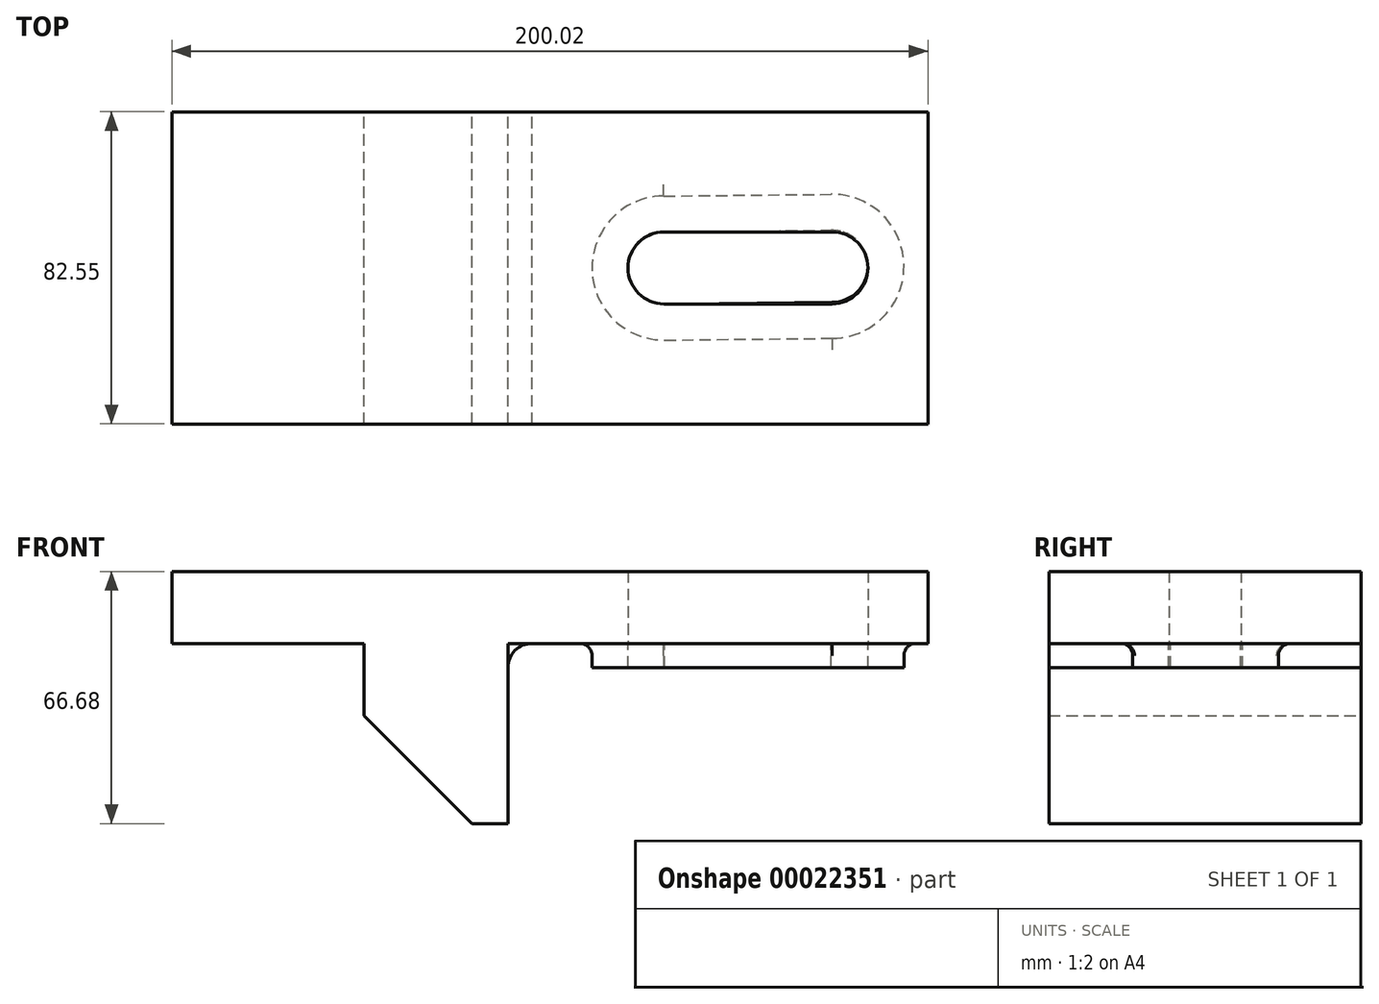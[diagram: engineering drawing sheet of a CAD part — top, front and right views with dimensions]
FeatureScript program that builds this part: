
annotation { "Feature Type Name" : "Feature", "Feature Type Description" : "" }
export const myFeature = defineFeature(function(context is Context, id is Id, definition is map)
    precondition{}
    {
        {
            var Q0;
            Q0=qCreatedBy(makeId("Top.planeOp"),FACE);
            var sketch = newSketch(context, id + "F0", { "sketchPlane" : qUnion([Q0])});
            skLineSegment(sketch, "E0.bottom", {"start": v(-105.1, 26.86) * mm, "end": v(94.93, 26.86) * mm});
            skLineSegment(sketch, "E0.top", {"start": v(-105.1, -55.7) * mm, "end": v(94.93, -55.7) * mm});
            skLineSegment(sketch, "E0.left", {"start": v(-105.1, 26.86) * mm, "end": v(-105.1, -55.7) * mm});
            skLineSegment(sketch, "E0.right", {"start": v(94.93, 26.86) * mm, "end": v(94.93, -55.7) * mm});
            skLineSegment(sketch, "E1.bottom", {"start": v(25.08, 4.63) * mm, "end": v(69.53, 4.63) * mm});
            skLineSegment(sketch, "E1.top", {"start": v(25.08, -33.47) * mm, "end": v(69.53, -33.47) * mm});
            skLineSegment(sketch, "E1.left", {"start": v(25.08, 4.63) * mm, "end": v(25.08, -33.47) * mm});
            skLineSegment(sketch, "E1.right", {"start": v(69.53, 4.63) * mm, "end": v(69.53, -33.47) * mm});
            skLineSegment(sketch, "E2.bottom", {"start": v(25.08, -4.9) * mm, "end": v(69.53, -4.9) * mm});
            skLineSegment(sketch, "E2.top", {"start": v(25.08, -23.94) * mm, "end": v(69.53, -23.94) * mm});
            skLineSegment(sketch, "E2.left", {"start": v(25.08, -4.9) * mm, "end": v(25.08, -23.94) * mm});
            skLineSegment(sketch, "E2.right", {"start": v(69.53, -4.9) * mm, "end": v(69.53, -23.94) * mm});
            skCircle(sketch, "E3", {"center": v(69.53, -14.42) * mm, "radius": 19.05 * mm});
            skCircle(sketch, "E4", {"center": v(25.08, -14.42) * mm, "radius": 19.05 * mm});
            skCircle(sketch, "E5", {"center": v(25.08, -14.42) * mm, "radius": 9.53 * mm});
            skCircle(sketch, "E6", {"center": v(69.53, -14.42) * mm, "radius": 9.53 * mm});
            skSolve(sketch);
        }
        {
            var Q0;
            Q0 = qSketchRegion(id + "F0", true);
            var Q1;
            {var subQ1=sQuery(id+"F0.wireOp",EDGE,"E1.left");var subQ5=sQuery(id+"F0.wireOp",EDGE,"E4");var subQ7=makeQuery(id+"F0.imprint","INTERSECT",VERTEX,{"derivedFrom":[sQuery(id+"F0.wireOp",EDGE,"E1.bottom"),subQ1,subQ5]});Q1=makeQuery(id+"F0.imprint","IMPRINT",FACE,{"disambiguationData":[TD([[makeQuery(id+"F0.imprint","IMPRINT",EDGE,{"disambiguationData":[TD([[subQ7,-1.0]])],"derivedFrom":subQ5}),1.0]])]});}
            var Q2;
            {var subQ3=sQuery(id+"F0.wireOp",EDGE,"E1.bottom");Q2=makeQuery(id+"F0.imprint","IMPRINT",FACE,{"disambiguationData":[TD([[makeQuery(id+"F0.imprint","IMPRINT",EDGE,{"derivedFrom":subQ3}),-1.0]])]});}
            var Q3;
            {var subQ1=sQuery(id+"F0.wireOp",EDGE,"E1.right");var subQ5=sQuery(id+"F0.wireOp",EDGE,"E3");var subQ7=makeQuery(id+"F0.imprint","INTERSECT",VERTEX,{"derivedFrom":[sQuery(id+"F0.wireOp",EDGE,"E1.bottom"),subQ1,subQ5]});Q3=makeQuery(id+"F0.imprint","IMPRINT",FACE,{"disambiguationData":[TD([[makeQuery(id+"F0.imprint","IMPRINT",EDGE,{"disambiguationData":[TD([[subQ7,1.0]])],"derivedFrom":subQ5}),1.0]])]});}
            var Q4;
            {var subQ0=sQuery(id+"F0.wireOp",EDGE,"E3");var subQ1=sQuery(id+"F0.wireOp",EDGE,"E2.bottom");var subQ2=makeQuery(id+"F0.imprint","INTERSECT",VERTEX,{"derivedFrom":[subQ1,subQ0]});Q4=makeQuery(id+"F0.imprint","IMPRINT",FACE,{"disambiguationData":[TD([[makeQuery(id+"F0.imprint","IMPRINT",EDGE,{"disambiguationData":[TD([[subQ2,1.0]])],"derivedFrom":subQ0}),1.0]])]});}
            var Q5;
            {var subQ0=sQuery(id+"F0.wireOp",EDGE,"E4");var subQ1=sQuery(id+"F0.wireOp",EDGE,"E2.bottom");var subQ2=makeQuery(id+"F0.imprint","INTERSECT",VERTEX,{"derivedFrom":[subQ1,subQ0]});Q5=makeQuery(id+"F0.imprint","IMPRINT",FACE,{"disambiguationData":[TD([[makeQuery(id+"F0.imprint","IMPRINT",EDGE,{"disambiguationData":[TD([[subQ2,-1.0]])],"derivedFrom":subQ0}),1.0]])]});}
            var Q6;
            {var subQ0=sQuery(id+"F0.wireOp",EDGE,"E4");var subQ1=sQuery(id+"F0.wireOp",EDGE,"E2.top");var subQ2=makeQuery(id+"F0.imprint","INTERSECT",VERTEX,{"derivedFrom":[subQ1,subQ0]});Q6=makeQuery(id+"F0.imprint","IMPRINT",FACE,{"disambiguationData":[TD([[makeQuery(id+"F0.imprint","IMPRINT",EDGE,{"disambiguationData":[TD([[subQ2,1.0]])],"derivedFrom":subQ0}),1.0]])]});}
            var Q7;
            {var subQ3=sQuery(id+"F0.wireOp",EDGE,"E1.top");Q7=makeQuery(id+"F0.imprint","IMPRINT",FACE,{"disambiguationData":[TD([[makeQuery(id+"F0.imprint","IMPRINT",EDGE,{"derivedFrom":subQ3}),1.0]])]});}
            var Q8;
            {var subQ0=sQuery(id+"F0.wireOp",EDGE,"E3");var subQ1=sQuery(id+"F0.wireOp",EDGE,"E2.top");var subQ2=makeQuery(id+"F0.imprint","INTERSECT",VERTEX,{"derivedFrom":[subQ1,subQ0]});Q8=makeQuery(id+"F0.imprint","IMPRINT",FACE,{"disambiguationData":[TD([[makeQuery(id+"F0.imprint","IMPRINT",EDGE,{"disambiguationData":[TD([[subQ2,-1.0]])],"derivedFrom":subQ0}),1.0]])]});}
            extrude(context, id + "F1", {"entities" : qUnion([Q0, Q1, Q2, Q3, Q4, Q5, Q6, Q7, Q8]), "depth" : 19.05 * mm});
        }
        {
            var Q0;
            Q0=qCreatedBy(makeId("Top.planeOp"),FACE);
            var sketch = newSketch(context, id + "F2", { "sketchPlane" : qUnion([Q0])});
            skCircle(sketch, "E7", {"center": v(25.08, -14.47) * mm, "radius": 19.05 * mm});
            skCircle(sketch, "E8", {"center": v(69.53, -14) * mm, "radius": 19.05 * mm});
            skLineSegment(sketch, "E9", {"start": v(25.05, 4.58) * mm, "end": v(69.34, 5.04) * mm});
            skLineSegment(sketch, "E10", {"start": v(25.3, -33.52) * mm, "end": v(69.54, -33.06) * mm});
            skLineSegment(sketch, "E11", {"start": v(25.08, -24) * mm, "end": v(25.3, -33.52) * mm});
            skLineSegment(sketch, "E12", {"start": v(25.08, -4.94) * mm, "end": v(25.05, 4.58) * mm});
            skLineSegment(sketch, "E13", {"start": v(69.34, 5.04) * mm, "end": v(69.53, -4.48) * mm});
            skLineSegment(sketch, "E14", {"start": v(69.54, -33.06) * mm, "end": v(69.53, -23.53) * mm});
            skLineSegment(sketch, "E15", {"start": v(25.08, -24) * mm, "end": v(69.53, -23.53) * mm});
            skLineSegment(sketch, "E16", {"start": v(25.08, -4.94) * mm, "end": v(69.53, -4.48) * mm});
            skCircle(sketch, "E17", {"center": v(25.08, -14.47) * mm, "radius": 9.53 * mm});
            skCircle(sketch, "E18", {"center": v(69.53, -14) * mm, "radius": 9.52 * mm});
            skSolve(sketch);
        }
        {
            var Q0;
            Q0 = qSketchRegion(id + "F2", true);
            var Q1;
            {var subQ3=sQuery(id+"F2.wireOp",EDGE,"E11");Q1=makeQuery(id+"F2.imprint","IMPRINT",FACE,{"disambiguationData":[TD([[makeQuery(id+"F2.imprint","IMPRINT",EDGE,{"derivedFrom":subQ3}),1.0]])]});}
            extrude(context, id + "F3", {"entities" : qUnion([Q0, Q1]), "operationType" : NewBodyOperationType.ADD, "oppositeDirection" : true, "depth" : 6.35 * mm});
        }
        {
            var Q0;
            Q0=makeQuery(id+"F1.opExtrude","SWEPT_FACE",FACE,{"disambiguationData":[OSD([sQuery(id+"F0.wireOp",EDGE,"E0.bottom")])]});
            var sketch = newSketch(context, id + "F4", { "sketchPlane" : qUnion([Q0])});
            skLineSegment(sketch, "E19", {"start": v(105.1, 0) * mm, "end": v(16.2, 0) * mm});
            skLineSegment(sketch, "E20", {"start": v(105.1, 0) * mm, "end": v(105.1, -47.63) * mm});
            skLineSegment(sketch, "E21.bottom", {"start": v(105.1, -47.63) * mm, "end": v(16.2, -47.63) * mm});
            skLineSegment(sketch, "E21.left", {"start": v(105.1, -47.63) * mm, "end": v(105.1, 0) * mm});
            skLineSegment(sketch, "E21.right", {"start": v(16.2, -47.63) * mm, "end": v(16.2, 0) * mm});
            skLineSegment(sketch, "E22", {"start": v(105.1, -47.63) * mm, "end": v(67, -47.63) * mm});
            skLineSegment(sketch, "E23", {"start": v(16.2, -47.63) * mm, "end": v(54.3, -47.63) * mm});
            skLineSegment(sketch, "E24", {"start": v(67, -47.63) * mm, "end": v(67, 0) * mm});
            skLineSegment(sketch, "E25", {"start": v(54.3, -47.63) * mm, "end": v(54.3, 0) * mm});
            skLineSegment(sketch, "E26", {"start": v(54.3, 0) * mm, "end": v(54.3, -12.7) * mm});
            skLineSegment(sketch, "E27", {"start": v(54.3, -12.7) * mm, "end": v(54.3, -19.05) * mm});
            skLineSegment(sketch, "E28", {"start": v(67, 0) * mm, "end": v(67, -12.7) * mm});
            skLineSegment(sketch, "E29", {"start": v(67, -12.7) * mm, "end": v(67, -19.05) * mm});
            skLineSegment(sketch, "E30", {"start": v(67, -12.7) * mm, "end": v(54.3, -12.7) * mm});
            skLineSegment(sketch, "E31", {"start": v(105.1, -47.63) * mm, "end": v(95.57, -47.63) * mm});
            skLineSegment(sketch, "E32", {"start": v(16.2, -47.63) * mm, "end": v(25.72, -47.63) * mm});
            skLineSegment(sketch, "E33", {"start": v(95.57, -47.63) * mm, "end": v(67, -19.05) * mm});
            skLineSegment(sketch, "E34", {"start": v(54.3, -19.05) * mm, "end": v(25.72, -47.63) * mm});
            skSolve(sketch);
        }
        {
            var Q0;
            {var subQ1=sQuery(id+"F4.wireOp",EDGE,"E21.left");Q0=makeQuery(id+"F4.imprint","IMPRINT",FACE,{"disambiguationData":[TD([[makeQuery(id+"F4.imprint","IMPRINT",EDGE,{"derivedFrom":subQ1}),1.0]])]});}
            var Q1;
            {var subQ1=sQuery(id+"F4.wireOp",EDGE,"E26");Q1=makeQuery(id+"F4.imprint","IMPRINT",FACE,{"disambiguationData":[TD([[makeQuery(id+"F4.imprint","IMPRINT",EDGE,{"derivedFrom":subQ1}),1.0]])]});}
            var Q2;
            {var subQ1=sQuery(id+"F4.wireOp",EDGE,"E21.right");Q2=makeQuery(id+"F4.imprint","IMPRINT",FACE,{"disambiguationData":[TD([[makeQuery(id+"F4.imprint","IMPRINT",EDGE,{"derivedFrom":subQ1}),-1.0]])]});}
            extrude(context, id + "F5", {"entities" : qUnion([Q0, Q1, Q2]), "operationType" : NewBodyOperationType.ADD, "oppositeDirection" : true, "depth" : 82.55 * mm});
        }
        {
            var Q0;
            Q0=makeQuery(id+"F5.boolean.opBoolean","MERGE",FACE,{"derivedFrom":[makeQuery(id+"F1.opExtrude","SWEPT_FACE",FACE,{"disambiguationData":[OSD([sQuery(id+"F0.wireOp",EDGE,"E0.bottom")])]}),makeQuery(id+"F5.opExtrude","CAP_FACE",FACE,{"disambiguationData":[OSD([sQuery(id+"F4.wireOp",EDGE,"E19"),sQuery(id+"F4.wireOp",EDGE,"E21.left"),sQuery(id+"F4.wireOp",EDGE,"E21.right"),sQuery(id+"F4.wireOp",EDGE,"E27"),sQuery(id+"F4.wireOp",EDGE,"E29"),sQuery(id+"F4.wireOp",EDGE,"E30"),sQuery(id+"F4.wireOp",EDGE,"E31"),sQuery(id+"F4.wireOp",EDGE,"E32"),sQuery(id+"F4.wireOp",EDGE,"E33"),sQuery(id+"F4.wireOp",EDGE,"E34")])],"isStart":true})]});
            var sketch = newSketch(context, id + "F6", { "sketchPlane" : qUnion([Q0])});
            skLineSegment(sketch, "E35", {"start": v(16.2, 0) * mm, "end": v(16.2, -6.35) * mm});
            skLineSegment(sketch, "E36", {"start": v(16.2, 0) * mm, "end": v(9.84, 0) * mm});
            skArc(sketch, "E37", {"start": v(16.2, -6.35) * mm, "mid": v(14.33, -1.86) * mm, "end": v(9.84, 0) * mm});
            skSolve(sketch);
        }
        {
            var Q0;
            Q0 = qSketchRegion(id + "F6", true);
            extrude(context, id + "F7", {"entities" : qUnion([Q0]), "oppositeDirection" : true, "depth" : 82.55 * mm});
        }
        {
            var Q0;
            Q0=makeQuery(id+"F3.opExtrude","CAP_EDGE",EDGE,{"disambiguationData":[OSD([sQuery(id+"F2.wireOp",EDGE,"E9")])],"isStart":true});
            var Q1;
            Q1=makeQuery(id+"F3.opExtrude","CAP_EDGE",EDGE,{"disambiguationData":[OSD([sQuery(id+"F2.wireOp",EDGE,"E8")])],"isStart":true});
            var Q2;
            Q2=makeQuery(id+"F3.opExtrude","CAP_EDGE",EDGE,{"disambiguationData":[OSD([sQuery(id+"F2.wireOp",EDGE,"E7")])],"isStart":true});
            var Q3;
            Q3=makeQuery(id+"F3.opExtrude","CAP_EDGE",EDGE,{"disambiguationData":[OSD([sQuery(id+"F2.wireOp",EDGE,"E10")])],"isStart":true});
            fillet(context, id + "F8", {"entities" : qUnion([Q0, Q1, Q2, Q3]), "radius" : 3.17 * mm, "allowEdgeOverflow" : false});
        }
    });
